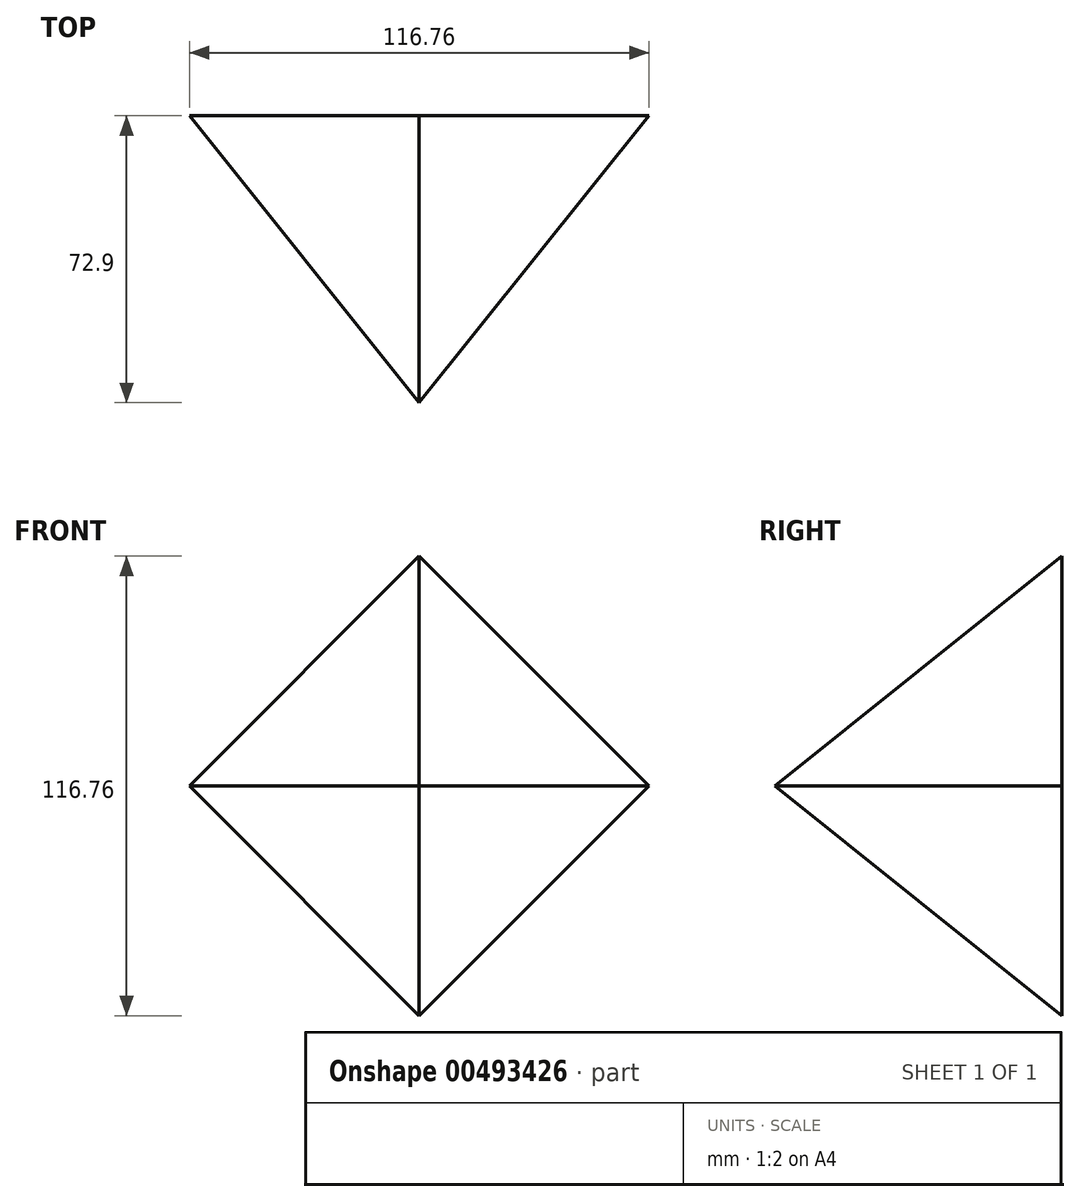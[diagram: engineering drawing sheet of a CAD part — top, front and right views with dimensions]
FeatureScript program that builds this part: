
annotation { "Feature Type Name" : "Feature", "Feature Type Description" : "" }
export const myFeature = defineFeature(function(context is Context, id is Id, definition is map)
    precondition{}
    {
        {
            var Q0;
            Q0=qCreatedBy(makeId("Front.planeOp"),FACE);
            var sketch = newSketch(context, id + "F0", { "sketchPlane" : qUnion([Q0])});
            skCircle(sketch, "E0.cCircle", {"center": v(0, 0) * mm, "radius": 58.38 * mm, "construction": true});
            skLineSegment(sketch, "E0.0", {"start": v(0, 58.38) * mm, "end": v(58.38, 0) * mm});
            skLineSegment(sketch, "E0.1", {"start": v(58.38, 0) * mm, "end": v(0, -58.38) * mm});
            skLineSegment(sketch, "E0.2", {"start": v(0, -58.38) * mm, "end": v(-58.38, 0) * mm});
            skLineSegment(sketch, "E0.3", {"start": v(-58.38, 0) * mm, "end": v(0, 58.38) * mm});
            skSolve(sketch);
        }
        {
            var Q0;
            Q0=qCreatedBy(makeId("Front.planeOp"),FACE);
            cPlane(context, id + "F1", {"entities" : qUnion([Q0]), "cplaneType" : CPlaneType.OFFSET, "offset" : 72.9 * mm, "width" : 150 * mm, "height" : 150 * mm});
        }
        {
            var Q0;
            Q0=qCreatedBy(id+"F1.planeOp",FACE);
            var sketch = newSketch(context, id + "F2", { "sketchPlane" : qUnion([Q0])});
            skPoint(sketch, "E1", {"position": v(0, 0) * mm});
            skSolve(sketch);
        }
        {
            var Q0;
            Q0=makeQuery(id+"F0.imprint","IMPRINT",FACE,{"disambiguationData":[TD([[makeQuery(id+"F0.imprint","IMPRINT",EDGE,{"derivedFrom":sQuery(id+"F0.wireOp",EDGE,"E0.0")}),-1.0]])]});
            var Q1;
            Q1=sQuery(id+"F2.wireOp",VERTEX,"E1");
            loft(context, id + "F3", {"sheetProfilesArray" : [{ "sheetProfileEntities" : qUnion([Q0]) }, { "sheetProfileEntities" : qUnion([Q1]) }]});
        }
    });
